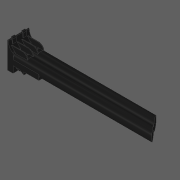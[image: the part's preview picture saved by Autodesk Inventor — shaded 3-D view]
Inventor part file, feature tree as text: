
AUTODESK INVENTOR PART (.ipt)
format: ipt  version: 2020 (Build 240168000, 168)  size: 1,066,496 bytes
history: native  units: in
note: dims shown in document units (in); Inventor stores cm internally (conversion verified against a paired STEP export)
features: other x33, extrude x19, loft x3, pattern_linear x3, fillet x2
ambient origin geometry x8: Origin, YZ Plane, XZ Plane, XY Plane, X Axis, Y Axis, Z Axis, Center Point
bodies: Body1 (feature_tree)
feature tree (60):
  other  "CrossSection1"
  other  "CrossSection2"
  other  "CrossSection3"
  other  "Whole"
  other  "Vertical Midplane"
  other  "Horizontal Midplane"
  extrude  "Block"  TaperAngle=0.0deg  [1 undecoded]
  extrude  "Hinge Protrusion"  Depth=0.7874in
  other  "Resonator Profile"
  extrude  "Resonator"  Depth=0.4724in
  extrude  "Resonator Cut"  Depth=0.3153in
  extrude  "Duct Cavity"  TaperAngle=0.0deg  [1 undecoded]
  other  "Duct Cavity Plane"
  loft  "Duct Entrance Loft"
  other  "Whistle Path Midplane"
  other  "Slit Loft To"
  loft  "Slit Loft"
  extrude  "Slit"  Depth=0.4882in
  other  "Fitting"
  extrude  "Edge Cut"  Depth=2.3498in
  other  "Edge Plane"
  other  "Edge Sketch"
  loft  "Edge Loft"
  extrude  "Edge"  Depth=0.1969in
  other  "Edge Cut Plane"
  extrude  "Spring Steel Slot"  Depth=0.1292in
  fillet  "Duct Fillet"  [1 undecoded]
  pattern_linear  "Channel Repetition"  Spacing1=0.2362in  [1 undecoded]
  extrude  "Edge Length Cut"  TaperAngle=0.0deg  [1 undecoded]
  other  "Tube Length Curve"
  extrude  "Tube Length Cut"  Depth=0.2441in
  extrude  "Whistle Walls"  Depth=0.1528in
  fillet  "Whistle Wall Fillet"  Radius=0.1245in
  pattern_linear  "Whistle Wall Repetition"  Spacing1=0.1528in  [1 undecoded]
  extrude  "End Caps"  Depth=0.2441in
  extrude  "Extra Block (for short notes)"  Depth=0.4921in
  other  "End Cap Tidying Plane"
  other  "End Cap Tidying Sketch"
  extrude  "End Cap Tidying"  Depth=0.0197in
  extrude  "End Cap Tidying (reverse)"  Depth=0.2559in
  pattern_linear  "End Cap Tidying Repetition"  Spacing1=0.8819in  [1 undecoded]
  extrude  "End Cap Tidying (edges)"  Depth=0.4882in
  extrude  "End Cap Tidying (edges, reverse)"  TaperAngle=0.0deg  [1 undecoded]
  other  "End-of-block Plane"
  extrude  "Manifold Slots"  Depth=0.2441in
  other  "Block Profile"
  other  "Fitting Sketch"
  other  "Duct Cavity Profile"
  other  "Duct Entrance Loft From"
  other  "Hinge Protrusion Sketch"
  other  "Edge Cut Sketch"
  other  "Edges3"
  other  "Edge Length Curve"
  other  "Whistle Wall Sketch"
  other  "2D Equation Curve10"
  other  "2D Equation Curve11"
  other  "Duct Entrance Loft To"
  other  "Slit Loft From"
  other  "Manifold Slot Sketch"
  other  "Spring Steel Slot Sketch"
note: 8 required parameter values undecoded (feature->parameter linkage not recoverable at this tier; creation-order binding heuristic only, values carry confidence <= 0.55)
